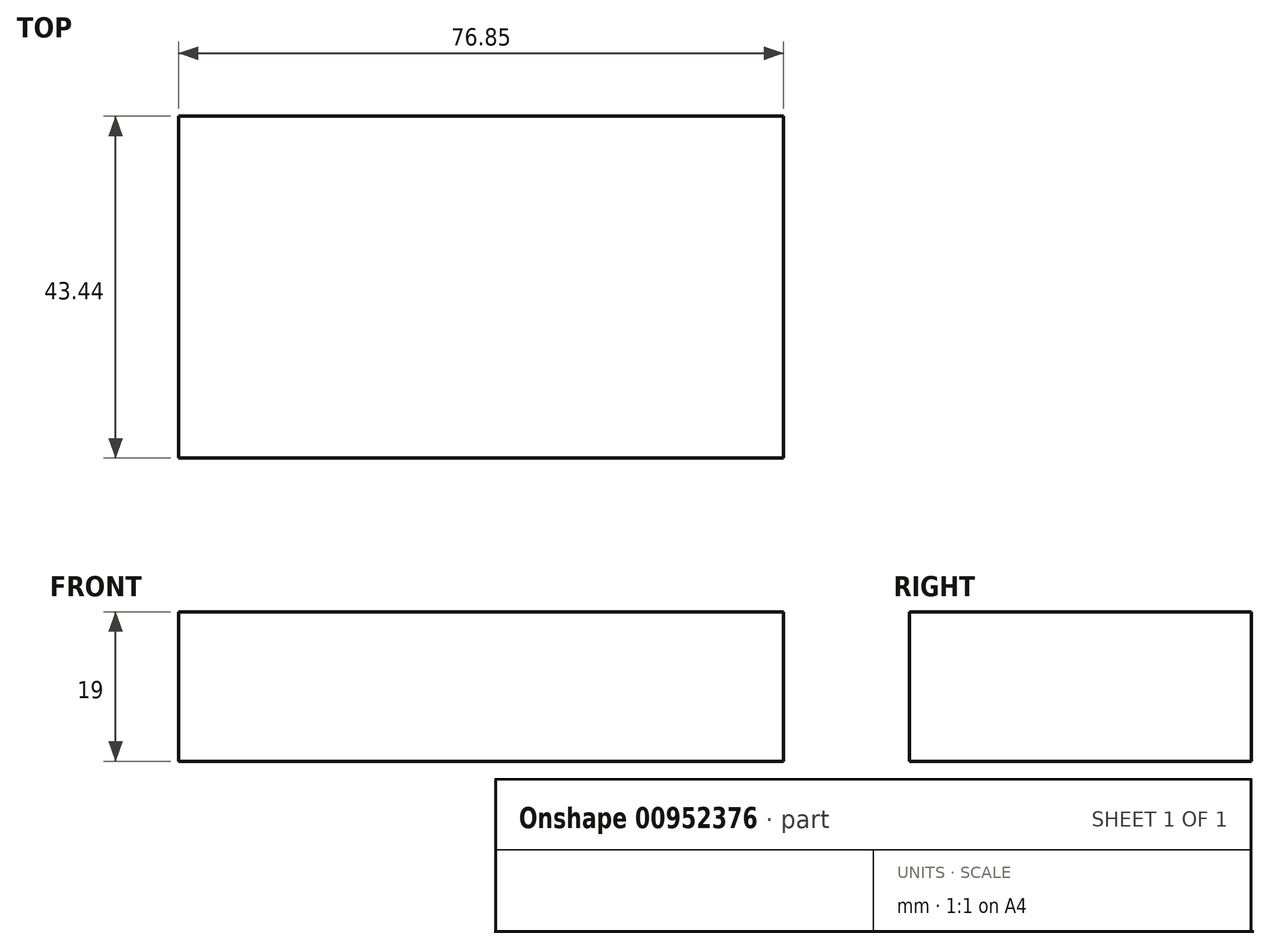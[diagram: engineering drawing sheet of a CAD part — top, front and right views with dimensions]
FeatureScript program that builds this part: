
annotation { "Feature Type Name" : "Feature", "Feature Type Description" : "" }
export const myFeature = defineFeature(function(context is Context, id is Id, definition is map)
    precondition{}
    {
        {
            var Q0;
            Q0=qCreatedBy(makeId("Top.planeOp"),FACE);
            var sketch = newSketch(context, id + "F0", { "sketchPlane" : qUnion([Q0])});
            skLineSegment(sketch, "E0.bottom", {"start": v(-29.07, 13.59) * mm, "end": v(47.78, 13.59) * mm});
            skLineSegment(sketch, "E0.top", {"start": v(-29.07, -29.85) * mm, "end": v(47.78, -29.85) * mm});
            skLineSegment(sketch, "E0.left", {"start": v(-29.07, 13.59) * mm, "end": v(-29.07, -29.85) * mm});
            skLineSegment(sketch, "E0.right", {"start": v(47.78, 13.59) * mm, "end": v(47.78, -29.85) * mm});
            skSolve(sketch);
        }
        {
            var Q0;
            Q0 = qSketchRegion(id + "F0", true);
            extrude(context, id + "F1", {"entities" : qUnion([Q0]), "depth" : 19 * mm, "offsetDistance" : 25 * mm});
        }
    });
